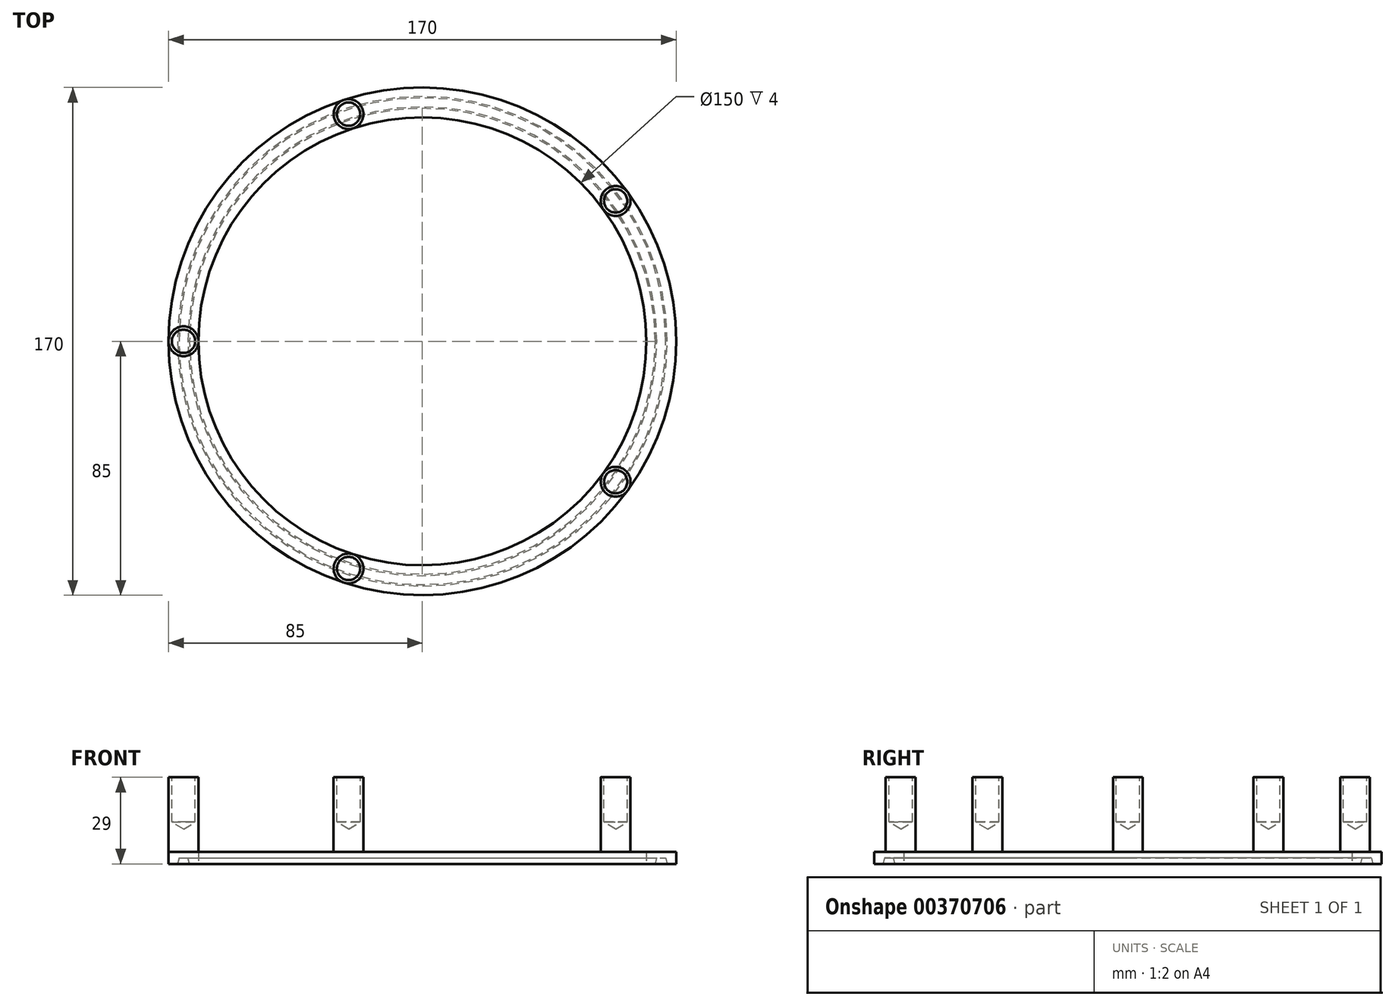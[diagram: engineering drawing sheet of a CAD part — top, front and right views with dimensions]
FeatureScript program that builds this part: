
annotation { "Feature Type Name" : "Feature", "Feature Type Description" : "" }
export const myFeature = defineFeature(function(context is Context, id is Id, definition is map)
    precondition{}
    {
        {
            assignVariable(context, id + "F0", {"name" : "D_loch", "anyValue" : 7.8});
        }
        {
            assignVariable(context, id + "F1", {"name" : "l_stuetze", "anyValue" : 25});
        }
        {
            assignVariable(context, id + "F2", {"name" : "l_bohrtiefe", "anyValue" : 15});
        }
        {
            var Q0;
            Q0=qCreatedBy(makeId("Top.planeOp"),FACE);
            var sketch = newSketch(context, id + "F3", { "sketchPlane" : qUnion([Q0])});
            skCircle(sketch, "E0", {"center": v(0, 0) * mm, "radius": 80 * mm, "construction": true});
            skSolve(sketch);
        }
        {
            var Q0;
            Q0=qCreatedBy(makeId("Front.planeOp"),FACE);
            var sketch = newSketch(context, id + "F4", { "sketchPlane" : qUnion([Q0])});
            skLineSegment(sketch, "E1.0", {"start": v(-80, 0) * mm, "end": v(80, 0) * mm, "construction": true});
            skLineSegment(sketch, "E2", {"start": v(78, -2) * mm, "end": v(75, -2) * mm});
            skLineSegment(sketch, "E3", {"start": v(75, -2) * mm, "end": v(75, 2) * mm});
            skLineSegment(sketch, "E4", {"start": v(75, 2) * mm, "end": v(80, 2) * mm});
            skLineSegment(sketch, "E5.MirrorCS", {"start": v(85, 2) * mm, "end": v(80, 2) * mm});
            skLineSegment(sketch, "E6.MirrorCS", {"start": v(85, -2) * mm, "end": v(85, 2) * mm});
            skLineSegment(sketch, "E7.MirrorCS", {"start": v(82, -2) * mm, "end": v(85, -2) * mm});
            skLineSegment(sketch, "E8", {"start": v(82, -2) * mm, "end": v(81.5, 0) * mm});
            skLineSegment(sketch, "E9", {"start": v(81.5, 0) * mm, "end": v(80, 0) * mm});
            skLineSegment(sketch, "E10", {"start": v(80, 0) * mm, "end": v(78.5, 0) * mm});
            skLineSegment(sketch, "E11", {"start": v(78.5, 0) * mm, "end": v(78, -2) * mm});
            skLineSegment(sketch, "E12", {"start": v(80, 0) * mm, "end": v(80, 2) * mm, "construction": true});
            skSolve(sketch);
        }
        {
            var Q0;
            Q0=makeQuery(id+"F4.imprint","IMPRINT",FACE,{"disambiguationData":[TD([[makeQuery(id+"F4.imprint","IMPRINT",EDGE,{"derivedFrom":sQuery(id+"F4.wireOp",EDGE,"E2")}),-1.0]])]});
            var Q1;
            Q1=sQuery(id+"F3.wireOp",EDGE,"E0");
            revolve(context, id + "F5", {"entities" : qUnion([Q0]), "axis" : qUnion([Q1]), "revolveType" : RevolveType.FULL});
        }
        {
            var Q0;
            Q0=makeQuery(id+"F5.opRevolve","SWEPT_FACE",FACE,{"disambiguationData":[OSD([sQuery(id+"F4.wireOp",EDGE,"E4"),sQuery(id+"F4.wireOp",EDGE,"E5.MirrorCS")])]});
            var sketch = newSketch(context, id + "F6", { "sketchPlane" : qUnion([Q0])});
            skCircle(sketch, "E13.cCircle", {"center": v(0, 0) * mm, "radius": 64.72 * mm, "construction": true});
            skLineSegment(sketch, "E13.0", {"start": v(-24.72, 76.08) * mm, "end": v(-80, 0) * mm, "construction": true});
            skLineSegment(sketch, "E13.1", {"start": v(64.72, 47.02) * mm, "end": v(-24.72, 76.08) * mm, "construction": true});
            skLineSegment(sketch, "E13.2", {"start": v(64.72, -47.02) * mm, "end": v(64.72, 47.02) * mm, "construction": true});
            skLineSegment(sketch, "E13.3", {"start": v(-24.72, -76.08) * mm, "end": v(64.72, -47.02) * mm, "construction": true});
            skLineSegment(sketch, "E13.4", {"start": v(-80, 0) * mm, "end": v(-24.72, -76.08) * mm, "construction": true});
            skPoint(sketch, "E13.0.midPoint", {"position": v(-52.36, 38.04) * mm});
            skLineSegment(sketch, "E14", {"start": v(-75, 0) * mm, "end": v(0, 0) * mm, "construction": true});
            skCircle(sketch, "E15.0", {"center": v(0, 0) * mm, "radius": 75 * mm});
            skLineSegment(sketch, "E16", {"start": v(-80, 0) * mm, "end": v(-75, 0) * mm, "construction": true});
            skLineSegment(sketch, "E17", {"start": v(-85, 0) * mm, "end": v(-80, 0) * mm, "construction": true});
            skSolve(sketch);
        }
        {
            var Q0;
            Q0=qCreatedBy(makeId("Right.planeOp"),FACE);
            var sketch = newSketch(context, id + "F7", { "sketchPlane" : qUnion([Q0])});
            skLineSegment(sketch, "E18", {"start": v(0, 0) * mm, "end": v(0, 65.63) * mm, "construction": true});
            skSolve(sketch);
        }
        {
            var Q0;
            Q0=makeQuery(id+"F6.imprint","IMPRINT",FACE,{"disambiguationData":[TD([[makeQuery(id+"F6.imprint","IMPRINT",EDGE,{"derivedFrom":sQuery(id+"F6.wireOp",EDGE,"E15.0")}),1.0]])]});
            var sketch = newSketch(context, id + "F8", { "sketchPlane" : qUnion([Q0])});
            skPoint(sketch, "E19.0", {"position": v(-24.72, 76.08) * mm});
            skPoint(sketch, "E19.1", {"position": v(64.72, 47.02) * mm});
            skPoint(sketch, "E19.2", {"position": v(64.72, -47.02) * mm});
            skPoint(sketch, "E19.3", {"position": v(-24.72, -76.08) * mm});
            skPoint(sketch, "E19.4", {"position": v(-80, 0) * mm});
            skCircle(sketch, "E20.0", {"center": v(0, 0) * mm, "radius": 75 * mm});
            skCircle(sketch, "E20.1", {"center": v(0, 0) * mm, "radius": 85 * mm});
            skCircle(sketch, "E21", {"center": v(-24.72, 76.08) * mm, "radius": 5 * mm});
            skSolve(sketch);
        }
        {
            var Q0;
            {var subQ0=sQuery(id+"F8.wireOp",EDGE,"E21");var subQ1=makeQuery(id+"F8.imprint","INTERSECT",VERTEX,{"derivedFrom":[sQuery(id+"F8.wireOp",EDGE,"E20.1"),subQ0]});Q0=makeQuery(id+"F8.imprint","IMPRINT",FACE,{"disambiguationData":[TD([[makeQuery(id+"F8.imprint","IMPRINT",EDGE,{"disambiguationData":[TD([[subQ1,-1.0]])],"derivedFrom":subQ0}),1.0]])]});}
            extrude(context, id + "F9", {"entities" : qUnion([Q0]), "depth" : (getVariable(context, 'l_stuetze')) * mm});
        }
        {
            var Q0;
            Q0=makeQuery(id+"F9.opExtrude","CAP_FACE",FACE,{"disambiguationData":[OSD([sQuery(id+"F8.wireOp",EDGE,"E21")])],"isStart":false});
            var sketch = newSketch(context, id + "F10", { "sketchPlane" : qUnion([Q0])});
            skPoint(sketch, "E22", {"position": v(-24.72, 76.08) * mm});
            skSolve(sketch);
        }
        {
            var Q0;
            Q0=sQuery(id+"F10.wireOp",VERTEX,"E22");
            var Q1;
            Q1=makeQuery(id+"F9.opExtrude","SWEPT_BODY",BODY,{"disambiguationData":[OSD([sQuery(id+"F8.wireOp",EDGE,"E21")])]});
            hole(context, id + "F11", {"style" : HoleStyle.SIMPLE, "endStyle" : HoleEndStyle.BLIND, "holeDiameter" : (getVariable(context, 'D_loch')) * mm, "holeDepth" : (getVariable(context, 'l_bohrtiefe')) * mm, "isTappedThrough" : true, "tappedDepth" : 12 * mm, "tapClearance" : 3, "locations" : qUnion([Q0]), "scope" : qUnion([Q1])});
        }
        {
            var Q0;
            Q0=makeQuery(id+"F9.opExtrude","SWEPT_BODY",BODY,{"disambiguationData":[OSD([sQuery(id+"F8.wireOp",EDGE,"E21")])]});
            var Q1;
            Q1=sQuery(id+"F7.wireOp",EDGE,"E18");
            circularPattern(context, id + "F12", {"entities" : qUnion([Q0]), "axis" : qUnion([Q1]), "angle" : 360 * degree, "instanceCount" : 5, "equalSpace" : true});
        }
    });
